# Revit family: 315L Outdoor Commercial Gas Storage Water Heater
name_source: partatom
category: Mechanical Equipment
revit_build: Autodesk Revit LT 2017 (Build: 20160225_1515(x64)
units: mm (PartAtom-declared; Revit-internal decimal feet)

## family parameters
Always vertical = Yes
Cut with Voids When Loaded = No
Part Type = Normal
Room Calculation Point = No
Round Connector Dimension = Use Diameter
Shared = No
Work Plane-Based = No

## types (1)
- Outdoor
    Cold Water Inlet  connector description = Cold Water Inlet connector: Male threaded connector R1-1/4"(DN32)
    Gas Inlet connector description = Gas Inlet Connector: Male threaded connector R¾”(DN20)
    Hot Water Outlet connector description = Hot Water Outlet connector: Male threaded connector R1-1/4"(DN32)
    No. of power supply point required = 1
    Nominal depth = 925mm
    Nominal gas consumption (MJ/h) = 220
    Nominal height = 1760mm
    Nominal width = 619mm
    Optional Cold Water Inlet connector description = Optional Cold Water Inlet connector: Male threaded connector R1-1/4"(DN32)
    Product SKU Dux brand = D12813EN/LTK
    Product SKU Thermann brand = T12813EN/LTK
    Product description = 315L Indoor Commercial Gas Storage Water Heater
    Total Maximum  power requirement(Watts) = 245
    Weight (Kg) = 139

## geometry (parser evidence)
native form markers: Sweep x2
no freeform markers — native parametric forms only
